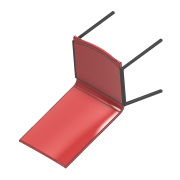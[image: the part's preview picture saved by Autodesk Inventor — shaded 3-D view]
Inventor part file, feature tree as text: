
AUTODESK INVENTOR PART (.ipt)
format: ipt  version: 2020.2 (Build 242310000, 310)  size: 469,504 bytes
history: native  units: mm
features: sketch x5, fillet x3, plane x2, extrude x2, loft x1
ambient origin geometry x8: Origin, YZ Plane, XZ Plane, XY Plane, X Axis, Y Axis, Z Axis, Center Point
bodies: Solid1 (feature_tree)
feature tree (13):
  sketch  "Sketch3"  dims[d0=600.0mm d1=19.198622mm]
  plane  "Work Plane2"
  plane  "Work Plane3"
  loft  "Loft1"
  extrude  "Extrusion1"  Depth=0.872665mm
  extrude  "Extrusion3"  Depth=50.0mm
  fillet  "Fillet3"  Radius=19.813101mm
  fillet  "Fillet4"  Radius=225.0mm
  fillet  "Fillet5"  Radius=20.0mm
  sketch  "Sketch6"  dims[d2=400.0mm d3=0.872665mm]
  sketch  "Sketch7"  dims[d4=2.0mm d5=50.0mm d6=19.813101mm d8=225.0mm d9=450.0mm]
  sketch  "Sketch9"  dims[d10=600.0mm d11=19.198622mm d12=400.0mm d13=0.872665mm d14=2.0mm d15=50.0mm d16=19.813101mm d17=20.0mm]
  sketch  "Sketch10"  dims[d18=20.0mm d19=600.0mm d20=19.198622mm d21=400.0mm d22=0.872665mm d23=2.0mm d24=50.0mm d25=19.813101mm d26=0.0mm d27=90.0deg d28=0.0mm d29=90.0deg d30=0.0mm d31=90.0deg d33=17.453293mm d39=20.0mm d41=400.0mm d42=14.3117mm d43=20.0mm d44=20.0mm d45=0.0mm d50=400.0mm d51=14.3117mm d52=20.0mm d53=20.0mm d54=0.0mm d55=5.0mm d56=5.0mm d57=5.0mm]
